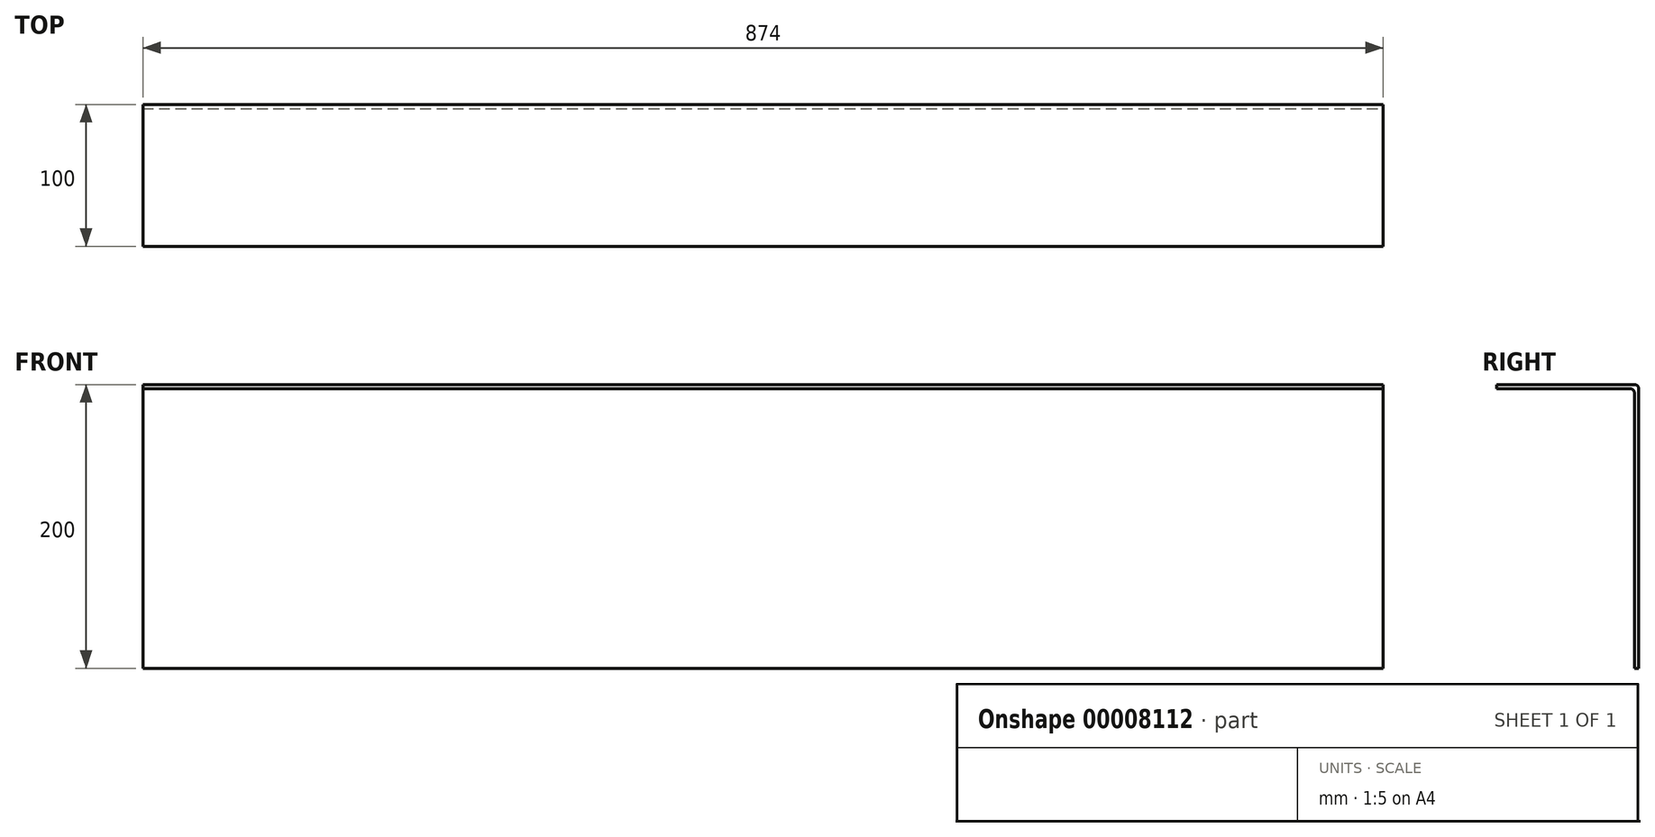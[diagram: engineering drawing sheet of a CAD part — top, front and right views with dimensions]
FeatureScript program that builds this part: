
annotation { "Feature Type Name" : "Feature", "Feature Type Description" : "" }
export const myFeature = defineFeature(function(context is Context, id is Id, definition is map)
    precondition{}
    {
        {
            var Q0;
            Q0=qCreatedBy(makeId("Right.planeOp"),FACE);
            var sketch = newSketch(context, id + "F0", { "sketchPlane" : qUnion([Q0])});
            skLineSegment(sketch, "E0", {"start": v(-97, 159.5) * mm, "end": v(3, 159.5) * mm});
            skLineSegment(sketch, "E1", {"start": v(3, 159.5) * mm, "end": v(3, -40.5) * mm});
            skLineSegment(sketch, "E2", {"start": v(3, -40.5) * mm, "end": v(0, -40.5) * mm});
            skLineSegment(sketch, "E3", {"start": v(0, -40.5) * mm, "end": v(0, 156.5) * mm});
            skLineSegment(sketch, "E4", {"start": v(0, 156.5) * mm, "end": v(-97, 156.5) * mm});
            skLineSegment(sketch, "E5", {"start": v(-97, 156.5) * mm, "end": v(-97, 159.5) * mm});
            skSolve(sketch);
        }
        {
            var Q0;
            Q0=makeQuery(id+"F0.imprint","IMPRINT",FACE,{"disambiguationData":[TD([[makeQuery(id+"F0.imprint","IMPRINT",EDGE,{"derivedFrom":sQuery(id+"F0.wireOp",EDGE,"E0")}),-1.0]])]});
            extrude(context, id + "F1", {"entities" : qUnion([Q0]), "oppositeDirection" : true, "depth" : 874 * mm});
        }
        {
            var Q0;
            Q0=makeQuery(id+"F1.opExtrude","SWEPT_EDGE",EDGE,{"disambiguationData":[OSD([sQuery(id+"F0.wireOp",EDGE,"E0"),sQuery(id+"F0.wireOp",EDGE,"E1")])]});
            var Q1;
            Q1=makeQuery(id+"F1.opExtrude","SWEPT_EDGE",EDGE,{"disambiguationData":[OSD([sQuery(id+"F0.wireOp",EDGE,"E3"),sQuery(id+"F0.wireOp",EDGE,"E4")])]});
            fillet(context, id + "F2", {"entities" : qUnion([Q0, Q1]), "radius" : 3 * mm, "tangentPropagation" : true, "allowEdgeOverflow" : false});
        }
    });
